# Revit family: Bleachers_Aluminum_15Row_Fixed
name_source: partatom
category: Generic Models
units: mm (PartAtom-declared; Revit-internal decimal feet)

## family parameters
Always vertical = Yes
Can host rebar = No
Classification Number = 23.40.50.11.11.11
Cut with Voids When Loaded = No
Maintain Annotation Orientation = No
Part Type = Normal
Room Calculation Point = No
Round Connector Dimension = Use Diameter
Shared = No
Work Plane-Based = No

## types (1)
- As Specified in Section 13 34 16
    Assembly Code = E2010500
    Construction Details = http://www.arcat.com
    Default Elevation = 0' - 0"
    Description = 15 Row Aluminum Belachers as specified in 13 34 16
    Expected Lifespan (Years) = 0
    Green Building-LEED = http://www.arcat.com
    Keynote = 13 34 16
    Length = 21' - 0"
    Live Load_Seating = 120.0000 psf
    Live Load_Structural = 100.0000 psf
    Maintenance Schedule (Months) = 0
    Manufacturer = Generic
    Manufacturer Fax = (203) 939-2444
    Manufacturer Website = http://www.arcat.com
    Model = Generic
    Product Data = http://www.arcat.com
    Product Properties = http://www.arcat.com
    Rows = 15
    Specification = http://www.arcat.com
    Warranty Duration (Years) = 0

## geometry (parser evidence)
native form markers: Blend x8, Sweep x3
no freeform markers — native parametric forms only
